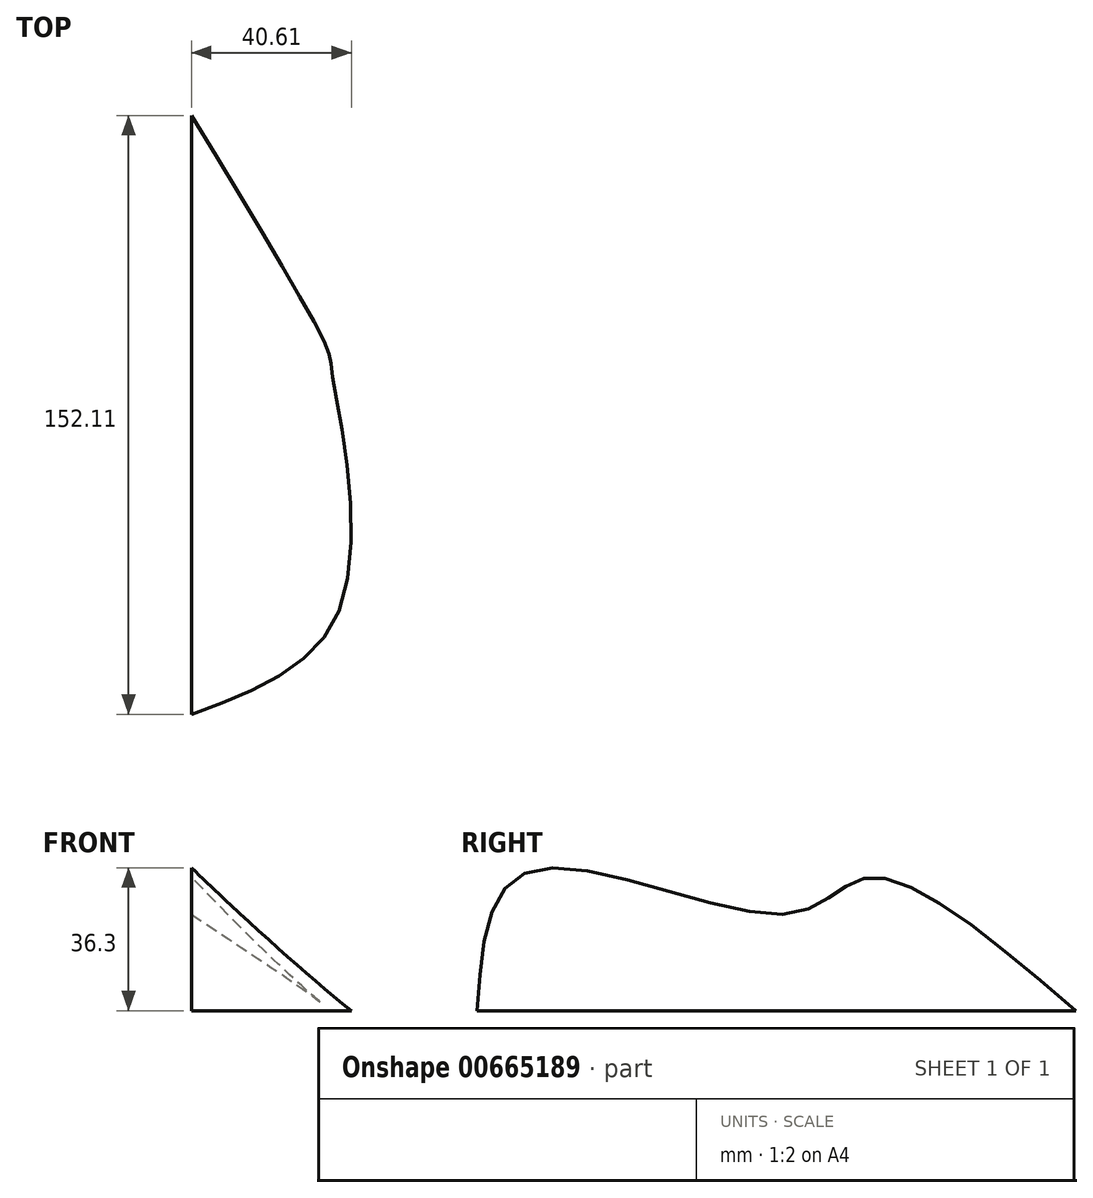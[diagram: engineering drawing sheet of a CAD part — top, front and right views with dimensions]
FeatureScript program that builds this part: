
annotation { "Feature Type Name" : "Feature", "Feature Type Description" : "" }
export const myFeature = defineFeature(function(context is Context, id is Id, definition is map)
    precondition{}
    {
        {
            var Q0;
            Q0=qCreatedBy(makeId("Top.planeOp"),FACE);
            var sketch = newSketch(context, id + "F0", { "sketchPlane" : qUnion([Q0])});
            skLineSegment(sketch, "E0", {"start": v(0, 0) * mm, "end": v(0, 152.11) * mm});
            skFitSpline(sketch, "E1", {"points": [v(0, 0) * mm, v(38.12, 28.07) * mm, v(35.81, 86.37) * mm, v(34.46, 92.97) * mm, v(0, 152.11) * mm], "startDerivative": vector(180.24, 65.56) * mm, "endDerivative": vector(-143.4, 235.07) * mm});
            skSolve(sketch);
        }
        {
            var Q0;
            Q0=qCreatedBy(makeId("Right.planeOp"),FACE);
            var sketch = newSketch(context, id + "F1", { "sketchPlane" : qUnion([Q0])});
            skLineSegment(sketch, "E2.0", {"start": v(0, 0) * mm, "end": v(152.11, 0) * mm});
            skFitSpline(sketch, "E3", {"points": [v(0, 0) * mm, v(13.7, 35.53) * mm, v(79.19, 24.6) * mm, v(99.42, 33.86) * mm, v(152.11, 0) * mm], "startDerivative": vector(13.78, 210) * mm, "endDerivative": vector(209.76, -179.43) * mm});
            skSolve(sketch);
        }
        {
            var Q0;
            Q0=sQuery(id+"F1.wireOp",EDGE,"E3");
            var Q1;
            Q1=sQuery(id+"F0.wireOp",EDGE,"E1");
            loft(context, id + "F2", {"bodyType" : ToolBodyType.SURFACE, "wireProfilesArray" : [{ "wireProfileEntities" : qUnion([Q0]) }, { "wireProfileEntities" : qUnion([Q1]) }]});
        }
    });
